# Revit family: DBLTD_TheSenatorGroup_OfficeChairs_Freeflow_US
name_source: partatom
category: Furniture
units: mm (PartAtom-declared; Revit-internal decimal feet)

## family parameters
Always vertical = Yes
Cut with Voids When Loaded = No
OmniClass Number = 23.40.20.00
OmniClass Title = General Furniture and Specialties
Render Appearance Source = Family Geometry
Room Calculation Point = No
Shared = Yes
Work Plane-Based = No

## types (3) — shared parameters
Assembly Code = E2020200
AssetType = Movable
Category = Pr_40_50_12_57 Office chairs
Color = Frame and base: Black, Light Grey. Back and seat: Onyx, Pearl, Ochre, Pine, Umber, Cliffside, Charcoal.
Constituents = Seat, Back and Frame
DurationUnit = years
ExpectedLife = 5
Finish = Frame and base: Black, Light Grey. Back and seat: Onyx, Pearl, Ochre, Pine, Umber, Cliffside, Charcoal.
Keynote = Pr_40_50_12_57 Office chairs
Manufacturer = The Senator Group
ManufacturerName = The Senator Group
ManufacturerURL = https://www.senator.online
Material = Frame and base: Nylon. Back and Seat: Upholstered PU foam.
Name = Chair
NominalDepth = 650 mm  [stored 2.13255 ft]
NominalHeight = 1160 mm  [stored 3.80577 ft]
NominalWidth = 650 mm  [stored 2.13255 ft]
ProductInformation = https://www.senator.online
SeatingHeight = 460 mm  [stored 1.50919 ft]
Shape = Rectangular
Size = 43-47.75 h x 25.5 w x 25.5 d "
URL = https://www.thesenatorgroup.com
Uniclass2015Code = Pr_40_50_12_57
Uniclass2015Title = Office chairs
Uniclass2015Version = Products v1.15
Version = 1
WarrantyDescription = The Senator Group warrants that its manufactured products are free from manufacturing defects - in materials or workmanship - for a period of five (5) years.
WarrantyDurationLabor = 5
WarrantyDurationParts = 5
WarrantyDurationUnit = years
WarrantyGuarantorLabor = https://www.allermuir.com
WarrantyGuarantorParts = https://www.allermuir.com
zero-valued in all types: Cost, Default Elevation

## per-type parameters (varying)
| type | ArmType | Model | ModelNumber |
| Task Chair without Arms | Nested_DBLTD_TheSenatorGroup_OfficeChairs_Freeflow_Arms : No Arms | FRF740-US | FRF740-US |
| Task Chair with Fixed Arms | Nested_DBLTD_TheSenatorGroup_OfficeChairs_Freeflow_Arms : Fixed Arms | FRF740A-US | FRF740A-US |
| Task Chair with Multi Function Arms | Nested_DBLTD_TheSenatorGroup_OfficeChairs_Freeflow_Arms : Multi Funcation Arms | FRF740MF-US | FRF740MF-US |

note: column(s) folded — value = type name in every type: Description, ModelReference, Type Comments

note: [stored X ft] marks values corroborated as IEEE doubles in the binary element streams (Revit-internal decimal feet)

## geometry (parser evidence)
native form markers: Sweep x10
no freeform markers — native parametric forms only
